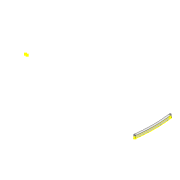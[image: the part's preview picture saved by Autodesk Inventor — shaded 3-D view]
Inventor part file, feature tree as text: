
AUTODESK INVENTOR PART (.ipt)
format: ipt  version: 2022 (Build 260153000, 153)  size: 98,816 bytes
history: native  units: mm
features: sketch x2, extrude x1, projected_geometry x1
ambient origin geometry x8: Origin, YZ Plane, XZ Plane, XY Plane, X Axis, Y Axis, Z Axis, Center Point
bodies: Solid1 (feature_tree)
feature tree (4):
  extrude  "Extrusion1"  Depth=111.226mm
  sketch  "Sketch2"  dims[d2=3.0mm d3=3.0mm d4=8.0mm d5=0.0mm d10=400.0mm d11=400.0mm]
  sketch  "Sketch1"  dims[d0=111.226mm d1=6.0mm]
  projected_geometry  "Projected Loop1"
